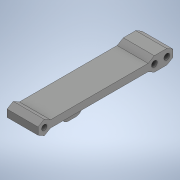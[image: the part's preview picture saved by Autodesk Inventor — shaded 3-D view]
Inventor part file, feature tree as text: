
AUTODESK INVENTOR PART (.ipt)
format: ipt  version: 2020 (Build 240168000, 168)  size: 352,256 bytes
history: native  units: in
note: dims shown in document units (in); Inventor stores cm internally (conversion verified against a paired STEP export)
features: sketch x6, extrude x5, projected_geometry x3, plane x2, mirror x1, fillet x1
ambient origin geometry x8: Origin, YZ Plane, XZ Plane, XY Plane, X Axis, Y Axis, Z Axis, Center Point
bodies: Solid1 (feature_tree)
feature tree (18):
  extrude  "Extrusion1"  Depth=3.4256in
  plane  "Work Plane1"
  extrude  "Extrusion2"  Depth=0.7874in
  sketch  "Sketch4"  dims[d4=0.0in d5=0.0827in]
  extrude  "Extrusion4"  Depth=0.0827in
  plane  "Work Plane2"
  extrude  "Extrusion6"  Depth=3.1106in
  mirror  "Mirror2"
  extrude  "Extrusion8"  Depth=0.315in
  fillet  "Fillet1"  Radius=0.1476in
  sketch  "Sketch1"  dims[d0=0.1818in d1=3.4256in]
  sketch  "Sketch2"  dims[d2=0.1378in d3=0.7874in]
  sketch  "Sketch5"  dims[d6=0.7874in d7=0.0in d28=3.1106in]
  sketch  "Sketch7"  dims[d29=0.315in d31=0.315in d33=0.1476in]
  projected_geometry  "Projected Loop7"
  projected_geometry  "Projected Loop8"
  sketch  "Sketch10"  dims[d34=0.2362in d35=0.0in d38=0.315in d39=0.2756in d40=-0.3092in d60=1.0994in d61=0.1378in d63=1.1811in d64=0.1575in d65=0.0in d66=0.126in d67=0.1575in]
  projected_geometry  "Projected Loop10"
